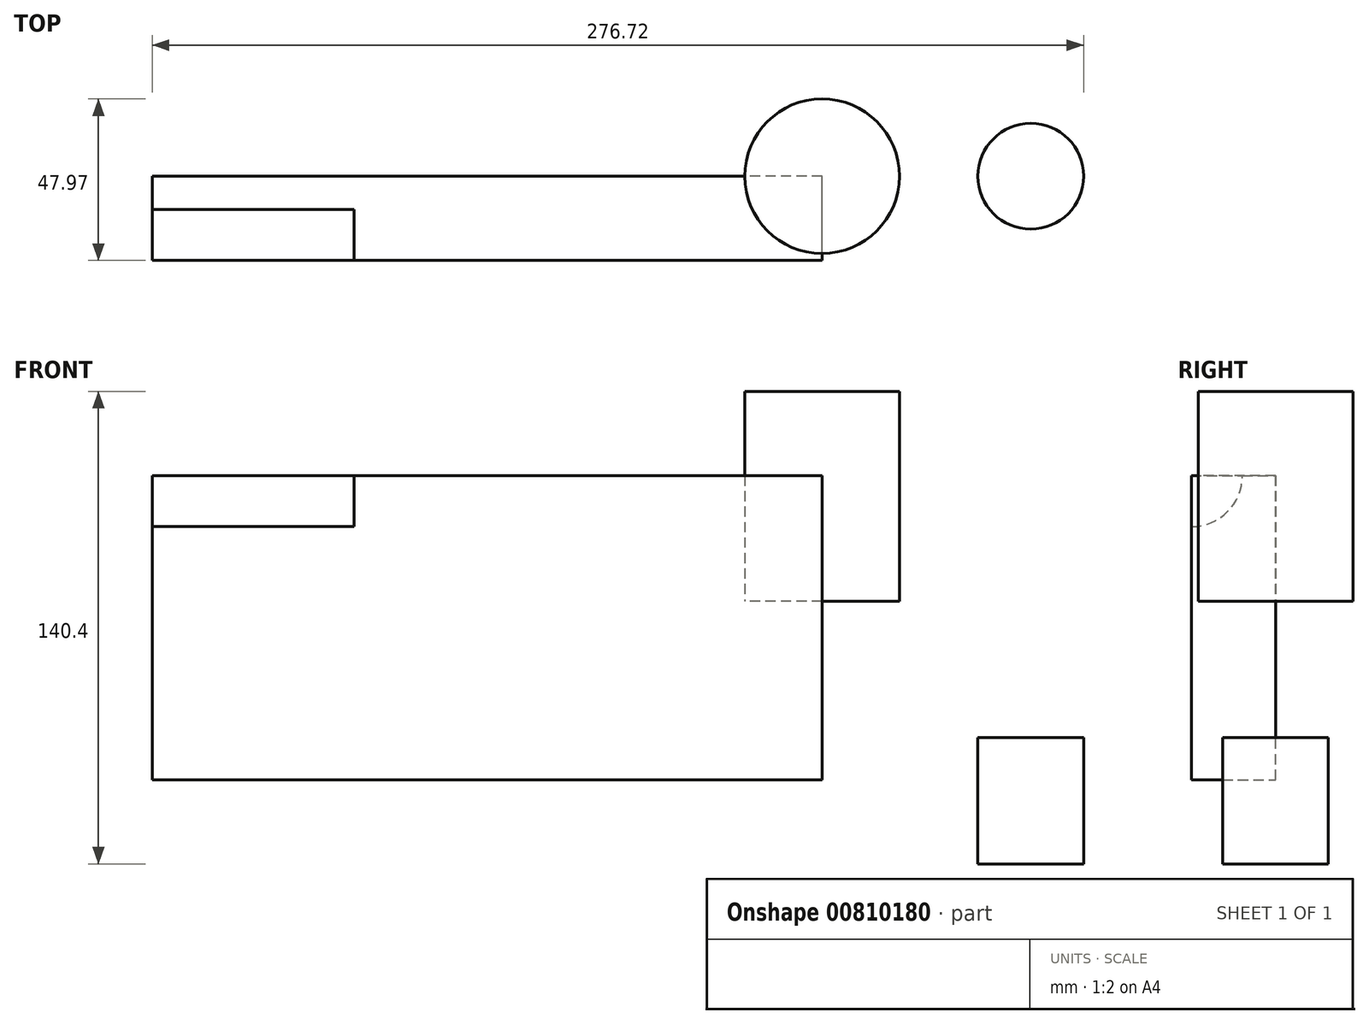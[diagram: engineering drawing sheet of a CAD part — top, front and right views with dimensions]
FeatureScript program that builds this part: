
annotation { "Feature Type Name" : "Feature", "Feature Type Description" : "" }
export const myFeature = defineFeature(function(context is Context, id is Id, definition is map)
    precondition{}
    {
        {
            var Q0;
            Q0=qCreatedBy(makeId("Front.planeOp"),FACE);
            var sketch = newSketch(context, id + "F0", { "sketchPlane" : qUnion([Q0])});
            skLineSegment(sketch, "E0.bottom", {"start": v(99.5, -45.2) * mm, "end": v(-99.5, -45.2) * mm});
            skLineSegment(sketch, "E0.top", {"start": v(99.5, 45.2) * mm, "end": v(-99.5, 45.2) * mm});
            skLineSegment(sketch, "E0.left", {"start": v(99.5, -45.2) * mm, "end": v(99.5, 45.2) * mm});
            skLineSegment(sketch, "E0.right", {"start": v(-99.5, -45.2) * mm, "end": v(-99.5, 45.2) * mm});
            skPoint(sketch, "E0.middle", {"position": v(0, 0) * mm});
            skSolve(sketch);
        }
        {
            var Q0;
            Q0=makeQuery(id+"F0.imprint","IMPRINT",FACE,{"disambiguationData":[TD([[makeQuery(id+"F0.imprint","IMPRINT",EDGE,{"derivedFrom":sQuery(id+"F0.wireOp",EDGE,"E0.bottom")}),-1.0]])]});
            extrude(context, id + "F1", {"entities" : qUnion([Q0]), "depth" : 25 * mm, "offsetDistance" : 25 * mm});
        }
        {
            var Q0;
            Q0=makeQuery(id+"F1.opExtrude","SWEPT_FACE",FACE,{"disambiguationData":[OSD([sQuery(id+"F0.wireOp",EDGE,"E0.top")])]});
            var sketch = newSketch(context, id + "F2", { "sketchPlane" : qUnion([Q0])});
            skCircle(sketch, "E1", {"center": v(99.5, 0) * mm, "radius": 22.97 * mm});
            skSolve(sketch);
        }
        {
            var Q0;
            Q0=makeQuery(id+"F1.opExtrude","SWEPT_FACE",FACE,{"disambiguationData":[OSD([sQuery(id+"F0.wireOp",EDGE,"E0.right")])]});
            var sketch = newSketch(context, id + "F3", { "sketchPlane" : qUnion([Q0])});
            skCircle(sketch, "E2", {"center": v(25, 45.2) * mm, "radius": 15.15 * mm});
            skSolve(sketch);
        }
        {
            var Q0;
            Q0 = qSketchRegion(id + "F3", true);
            extrude(context, id + "F4", {"entities" : qUnion([Q0]), "operationType" : NewBodyOperationType.REMOVE, "oppositeDirection" : true, "depth" : 60 * mm, "offsetDistance" : 25 * mm});
        }
        {
            var Q0;
            Q0 = qSketchRegion(id + "F2", true);
            extrude(context, id + "F5", {"entities" : qUnion([Q0]), "operationType" : NewBodyOperationType.ADD, "depth" : 25 * mm, "offsetDistance" : 25 * mm});
        }
        {
            var Q0;
            Q0 = qSketchRegion(id + "F2", true);
            extrude(context, id + "F6", {"entities" : qUnion([Q0]), "operationType" : NewBodyOperationType.ADD, "depth" : 25 * mm, "offsetDistance" : 25 * mm, "hasSecondDirection" : true, "secondDirectionOppositeDirection" : true, "secondDirectionDepth" : 37.4 * mm});
        }
        {
            var Q0;
            Q0=makeQuery(id+"F1.opExtrude","SWEPT_FACE",FACE,{"disambiguationData":[OSD([sQuery(id+"F0.wireOp",EDGE,"E0.bottom")])]});
            var sketch = newSketch(context, id + "F7", { "sketchPlane" : qUnion([Q0])});
            skCircle(sketch, "E3", {"center": v(99.5, 0) * mm, "radius": 15.72 * mm});
            skSolve(sketch);
        }
        {
            var Q0;
            Q0 = qSketchRegion(id + "F7", true);
            extrude(context, id + "F8", {"entities" : qUnion([Q0]), "depth" : 25 * mm, "offsetDistance" : 25 * mm, "hasSecondDirection" : true, "secondDirectionOppositeDirection" : true, "secondDirectionDepth" : 12.5 * mm});
        }
        {
            var Q0;
            Q0=makeQuery(id+"F8.opExtrude","SWEPT_BODY",BODY,{"disambiguationData":[OSD([sQuery(id+"F7.wireOp",EDGE,"E3")])]});
            transform(context, id + "F9", {"entities" : qUnion([Q0]), "transformType" : TransformType.TRANSLATION_3D, "dx" : 62 * mm, "dy" : 0 * mm, "dz" : 0 * mm, "makeCopy" : false});
        }
    });
